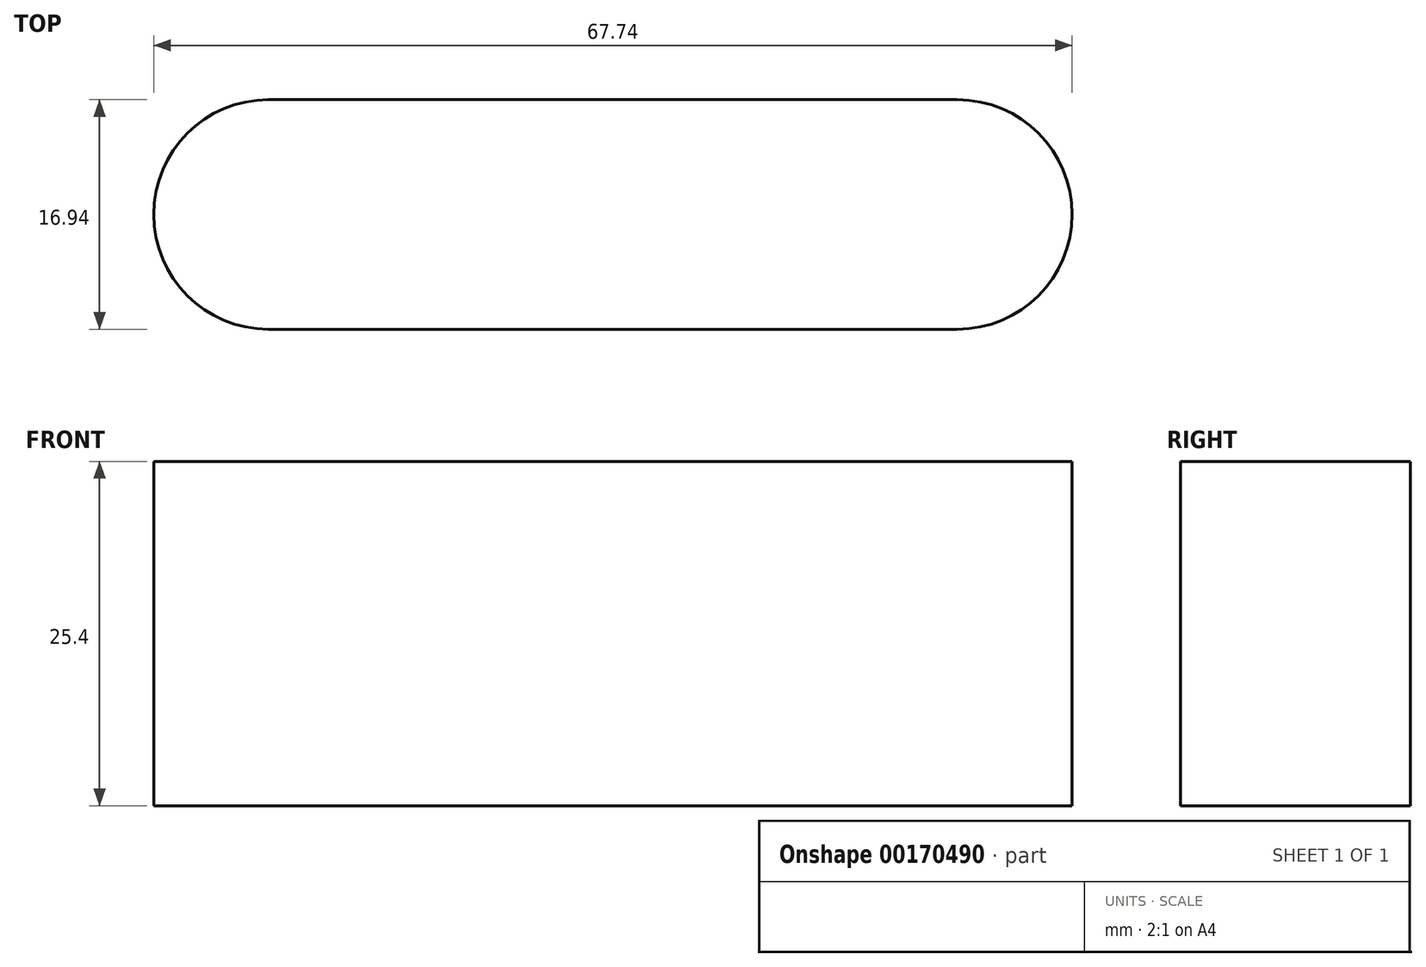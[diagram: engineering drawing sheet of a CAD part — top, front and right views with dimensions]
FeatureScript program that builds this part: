
annotation { "Feature Type Name" : "Feature", "Feature Type Description" : "" }
export const myFeature = defineFeature(function(context is Context, id is Id, definition is map)
    precondition{}
    {
        {
            var Q0;
            Q0=qCreatedBy(makeId("Top.planeOp"),FACE);
            var sketch = newSketch(context, id + "F0", { "sketchPlane" : qUnion([Q0])});
            skLineSegment(sketch, "E0.bottom", {"start": v(-25.4, 8.47) * mm, "end": v(25.4, 8.47) * mm});
            skLineSegment(sketch, "E0.top", {"start": v(-25.4, -8.47) * mm, "end": v(25.4, -8.47) * mm});
            skLineSegment(sketch, "E0.left", {"start": v(-25.4, 8.47) * mm, "end": v(-25.4, -8.47) * mm});
            skLineSegment(sketch, "E0.right", {"start": v(25.4, 8.47) * mm, "end": v(25.4, -8.47) * mm});
            skPoint(sketch, "E0.middle", {"position": v(0, 0) * mm});
            skArc(sketch, "E1", {"start": v(25.4, -8.47) * mm, "mid": v(33.87, 0) * mm, "end": v(25.4, 8.47) * mm});
            skArc(sketch, "E2", {"start": v(-25.4, 8.47) * mm, "mid": v(-33.87, 0) * mm, "end": v(-25.4, -8.47) * mm});
            skSolve(sketch);
        }
        {
            var Q0;
            Q0 = qSketchRegion(id + "F0", true);
            extrude(context, id + "F1", {"entities" : qUnion([Q0]), "depth" : 25.4 * mm});
        }
    });
